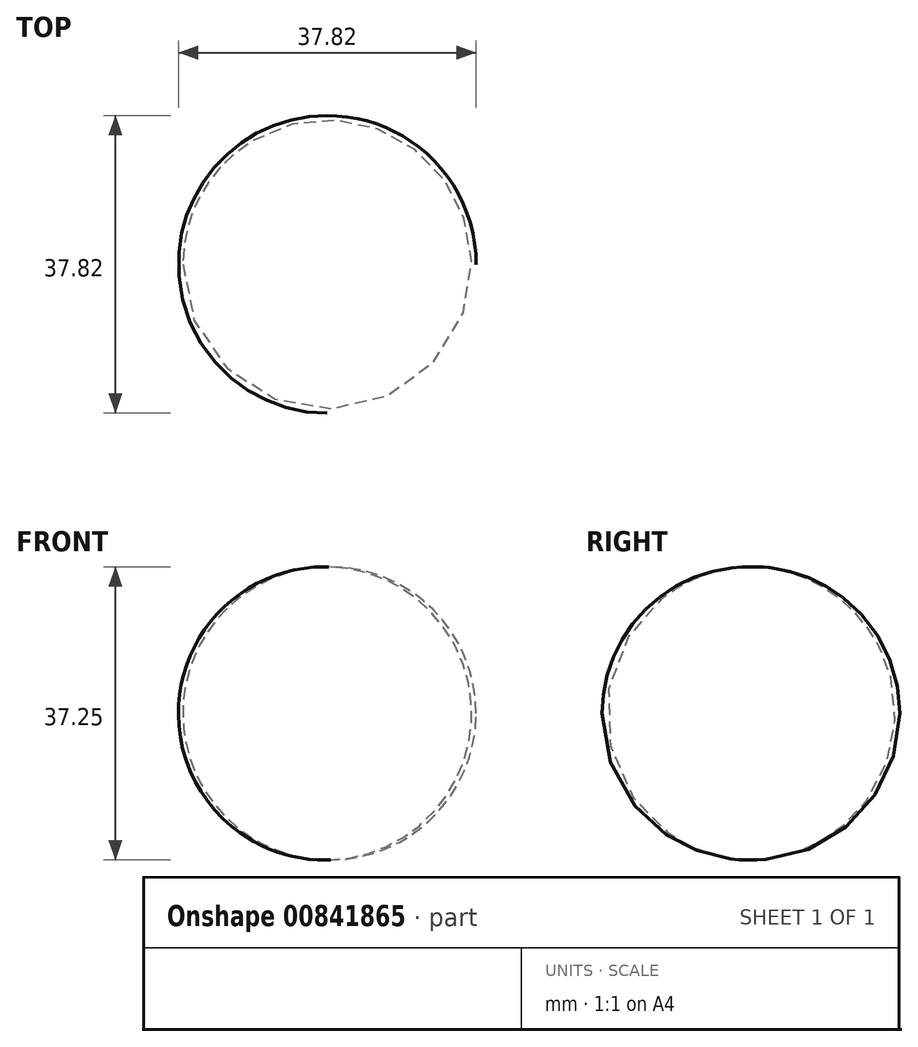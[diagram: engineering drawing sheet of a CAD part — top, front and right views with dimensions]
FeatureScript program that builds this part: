
annotation { "Feature Type Name" : "Feature", "Feature Type Description" : "" }
export const myFeature = defineFeature(function(context is Context, id is Id, definition is map)
    precondition{}
    {
        {
            var Q0;
            Q0=qCreatedBy(makeId("Front.planeOp"),FACE);
            var sketch = newSketch(context, id + "F0", { "sketchPlane" : qUnion([Q0])});
            skArc(sketch, "E0", {"start": v(-49.19, 37.24) * mm, "mid": v(-67.4, 18.5) * mm, "end": v(-48.93, 0) * mm});
            skLineSegment(sketch, "E1", {"start": v(-49.19, 37.24) * mm, "end": v(-48.93, 0) * mm});
            skSolve(sketch);
        }
        {
            var Q0;
            Q0=makeQuery(id+"F0.imprint","IMPRINT",FACE,{"disambiguationData":[TD([[makeQuery(id+"F0.imprint","IMPRINT",EDGE,{"derivedFrom":sQuery(id+"F0.wireOp",EDGE,"E0")}),1.0]])]});
            var Q1;
            Q1=sQuery(id+"F0.wireOp",EDGE,"E1");
            revolve(context, id + "F1", {"surfaceOperationType" : NewSurfaceOperationType.NEW, "entities" : qUnion([Q0]), "axis" : qUnion([Q1]), "revolveType" : RevolveType.FULL});
        }
    });
